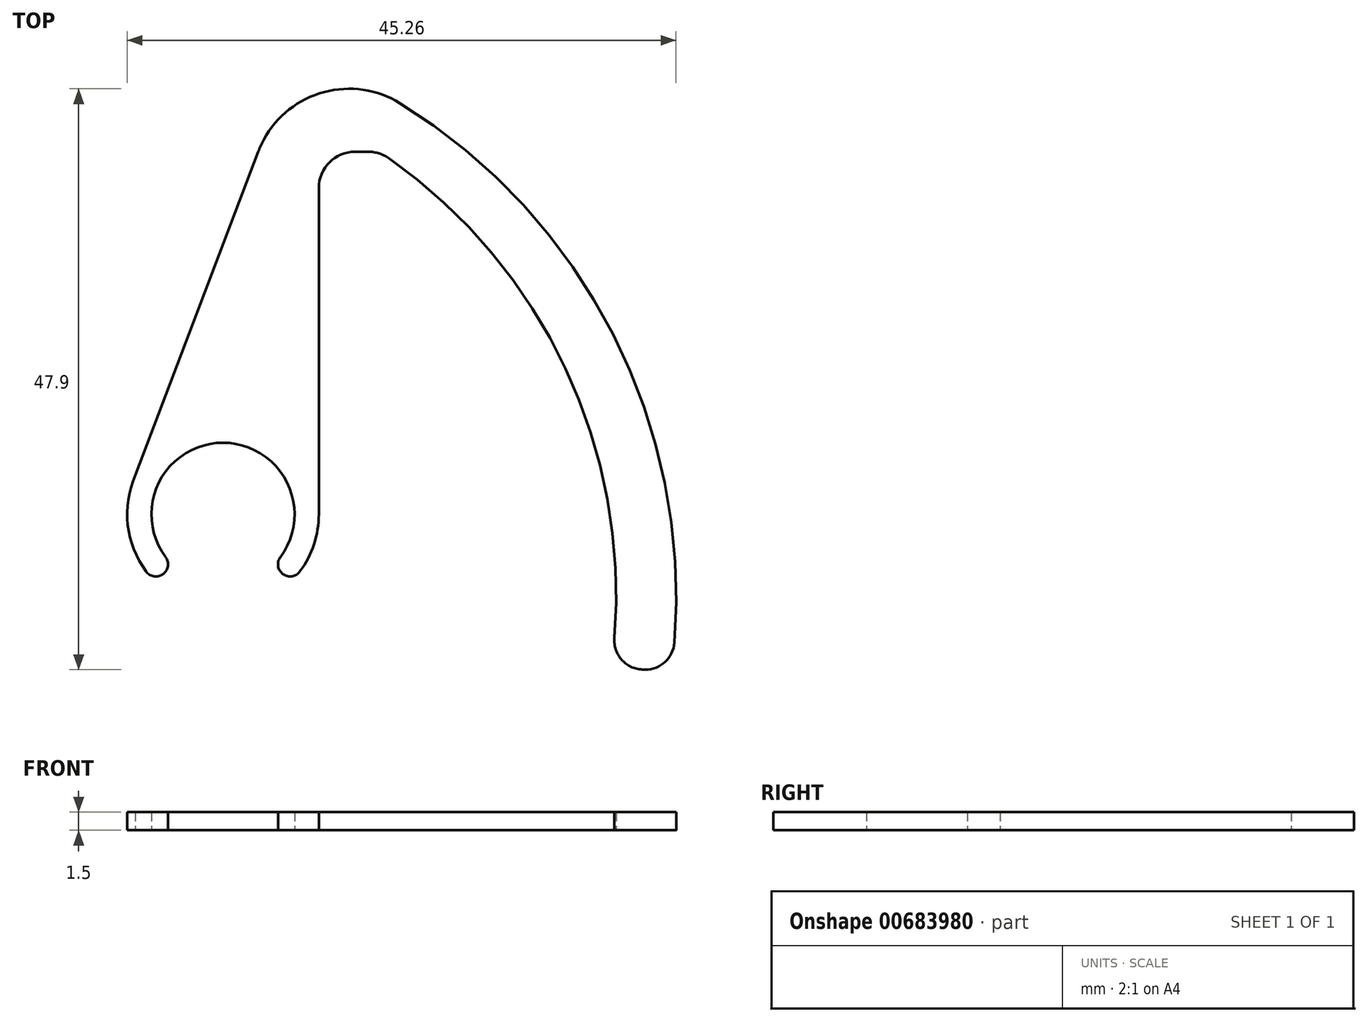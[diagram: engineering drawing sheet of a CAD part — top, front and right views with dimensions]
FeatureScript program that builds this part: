
annotation { "Feature Type Name" : "Feature", "Feature Type Description" : "" }
export const myFeature = defineFeature(function(context is Context, id is Id, definition is map)
    precondition{}
    {
        {
            var Q0;
            Q0=qCreatedBy(makeId("Top.planeOp"),FACE);
            var sketch = newSketch(context, id + "F0", { "sketchPlane" : qUnion([Q0])});
            skArc(sketch, "E0", {"start": v(4.17, -4.17) * mm, "mid": v(0, 5.9) * mm, "end": v(-4.17, -4.17) * mm});
            skArc(sketch, "E1", {"start": v(5.59, -5.59) * mm, "mid": v(0, 7.9) * mm, "end": v(-5.59, -5.59) * mm});
            skLineSegment(sketch, "E2", {"start": v(0, 0) * mm, "end": v(5.9, 0) * mm});
            skLineSegment(sketch, "E3", {"start": v(7.9, 0) * mm, "end": v(7.9, 29.9) * mm});
            skLineSegment(sketch, "E4", {"start": v(-7.22, 3.21) * mm, "end": v(2.9, 29.9) * mm});
            skLineSegment(sketch, "E5", {"start": v(2.9, 29.9) * mm, "end": v(7.9, 29.9) * mm});
            skLineSegment(sketch, "E6", {"start": v(4.17, -4.17) * mm, "end": v(5.59, -5.59) * mm});
            skLineSegment(sketch, "E7", {"start": v(-4.17, -4.17) * mm, "end": v(-5.59, -5.59) * mm});
            skLineSegment(sketch, "E8", {"start": v(7.9, 29.9) * mm, "end": v(12.9, 29.9) * mm});
            skArc(sketch, "E9", {"start": v(32, -12.8) * mm, "mid": v(28.57, 11.29) * mm, "end": v(12.9, 29.9) * mm});
            skArc(sketch, "E10", {"start": v(37, -12.8) * mm, "mid": v(32.22, 14.72) * mm, "end": v(12.9, 34.9) * mm});
            skArc(sketch, "E11", {"start": v(12.9, 34.9) * mm, "mid": v(6.92, 34.35) * mm, "end": v(2.9, 29.9) * mm});
            skLineSegment(sketch, "E12", {"start": v(32, -12.8) * mm, "end": v(37, -12.8) * mm});
            skSolve(sketch);
        }
        {
            var Q0;
            {var subQ0=sQuery(id+"F0.wireOp",EDGE,"E3");Q0=makeQuery(id+"F0.imprint","IMPRINT",FACE,{"disambiguationData":[TD([[makeQuery(id+"F0.imprint","IMPRINT",EDGE,{"derivedFrom":subQ0}),1.0]])]});}
            var Q1;
            Q1=makeQuery(id+"F0.imprint","IMPRINT",FACE,{"disambiguationData":[TD([[makeQuery(id+"F0.imprint","IMPRINT",EDGE,{"derivedFrom":sQuery(id+"F0.wireOp",EDGE,"E5")}),1.0]])]});
            var Q2;
            {var subQ3=sQuery(id+"F0.wireOp",EDGE,"E6");Q2=makeQuery(id+"F0.imprint","IMPRINT",FACE,{"disambiguationData":[TD([[makeQuery(id+"F0.imprint","IMPRINT",EDGE,{"derivedFrom":subQ3}),1.0]])]});}
            extrude(context, id + "F1", {"entities" : qUnion([Q0, Q1, Q2]), "depth" : 1.5 * mm, "offsetDistance" : 25 * mm});
        }
        {
            var Q0;
            Q0=makeQuery(id+"F1.opExtrude","SWEPT_EDGE",EDGE,{"disambiguationData":[OSD([sQuery(id+"F0.wireOp",EDGE,"E3"),sQuery(id+"F0.wireOp",EDGE,"E5"),sQuery(id+"F0.wireOp",EDGE,"E8")])]});
            var Q1;
            Q1=makeQuery(id+"F1.opExtrude","SWEPT_EDGE",EDGE,{"disambiguationData":[OSD([sQuery(id+"F0.wireOp",EDGE,"E8"),sQuery(id+"F0.wireOp",EDGE,"E9")])]});
            fillet(context, id + "F2", {"entities" : qUnion([Q0, Q1]), "radius" : 3 * mm, "tangentPropagation" : true, "allowEdgeOverflow" : false});
        }
        {
            var Q0;
            Q0=makeQuery(id+"F1.opExtrude","SWEPT_EDGE",EDGE,{"disambiguationData":[OSD([sQuery(id+"F0.wireOp",EDGE,"E9"),sQuery(id+"F0.wireOp",EDGE,"E12")])]});
            var Q1;
            Q1=makeQuery(id+"F1.opExtrude","SWEPT_EDGE",EDGE,{"disambiguationData":[OSD([sQuery(id+"F0.wireOp",EDGE,"E10"),sQuery(id+"F0.wireOp",EDGE,"E12")])]});
            fillet(context, id + "F3", {"entities" : qUnion([Q0, Q1]), "radius" : 2.4 * mm, "tangentPropagation" : true, "allowEdgeOverflow" : false});
        }
        {
            var Q0;
            Q0=makeQuery(id+"F1.opExtrude","SWEPT_EDGE",EDGE,{"disambiguationData":[OSD([sQuery(id+"F0.wireOp",EDGE,"E0"),sQuery(id+"F0.wireOp",EDGE,"E6")])]});
            var Q1;
            Q1=makeQuery(id+"F1.opExtrude","SWEPT_EDGE",EDGE,{"disambiguationData":[OSD([sQuery(id+"F0.wireOp",EDGE,"E0"),sQuery(id+"F0.wireOp",EDGE,"E7")])]});
            var Q2;
            Q2=makeQuery(id+"F1.opExtrude","SWEPT_EDGE",EDGE,{"disambiguationData":[OSD([sQuery(id+"F0.wireOp",EDGE,"E1"),sQuery(id+"F0.wireOp",EDGE,"E6")])]});
            var Q3;
            Q3=makeQuery(id+"F1.opExtrude","SWEPT_EDGE",EDGE,{"disambiguationData":[OSD([sQuery(id+"F0.wireOp",EDGE,"E1"),sQuery(id+"F0.wireOp",EDGE,"E7")])]});
            fillet(context, id + "F4", {"entities" : qUnion([Q0, Q1, Q2, Q3]), "radius" : 1 * mm, "tangentPropagation" : true, "allowEdgeOverflow" : false});
        }
        {
            var Q0;
            Q0=makeQuery(id+"F1.opExtrude","SWEPT_EDGE",EDGE,{"disambiguationData":[OSD([sQuery(id+"F0.wireOp",EDGE,"E10"),sQuery(id+"F0.wireOp",EDGE,"E11")])]});
            fillet(context, id + "F5", {"entities" : qUnion([Q0]), "radius" : 8 * mm, "tangentPropagation" : true, "allowEdgeOverflow" : false});
        }
    });
